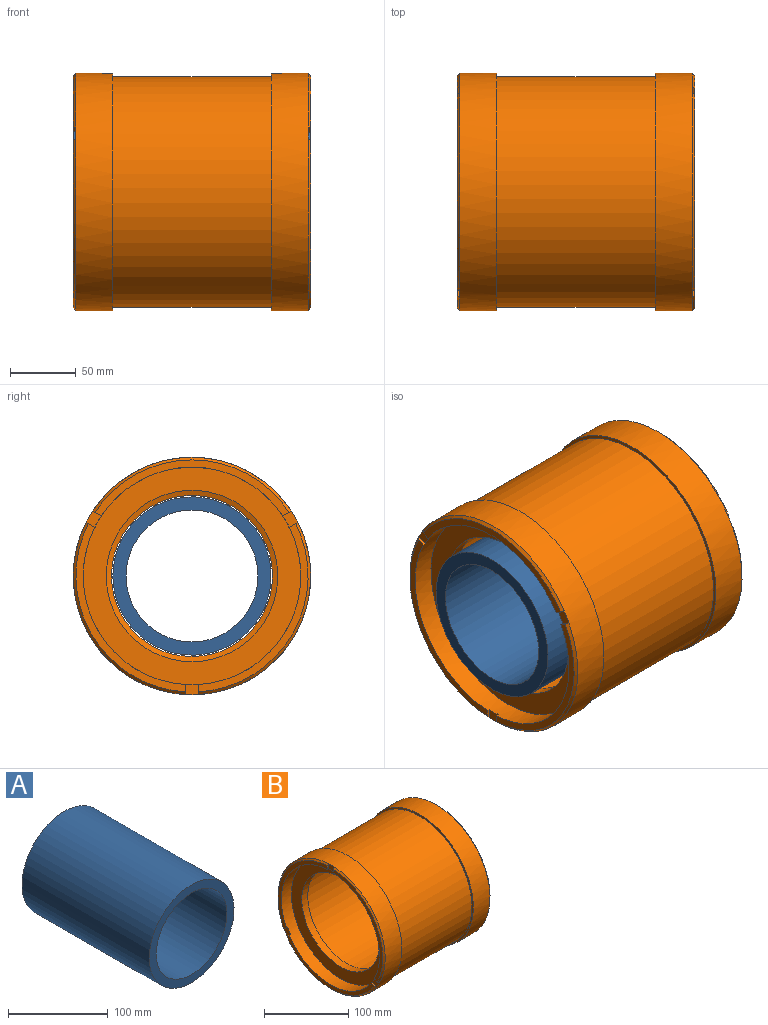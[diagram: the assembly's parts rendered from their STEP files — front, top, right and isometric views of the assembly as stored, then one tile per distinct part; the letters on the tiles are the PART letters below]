
ASSEMBLY  parts=2 mates=1
PART A: 4 faces, bbox 120x180x120 mm
  f0: cylinder r=50mm len=180mm, axis (0,1,0), area 56548.7mm2, adj f2,f3
  f1: cylinder r=60mm len=180mm, axis (0,1,0), area 67858.4mm2, adj f2,f3
  f2: plane 120x120mm, normal (0,-1,0), area 3455.8mm2, adj f0,f1
  f3: plane 120x120mm, normal (0,1,0), area 3455.8mm2, adj f0,f1
PART B: 45 faces, bbox 180x180x180 mm
  f0: plane 127.46x83mm, normal (-1,0,0), area 927mm2, adj f2,f13,f39,f43
  f1: plane 147.17x42.5mm, normal (-1,0,0), area 927mm2, adj f3,f13,f36,f40
  f2: cone r=88mm half-angle=45deg, axis (1,0,0), area 498.9mm2, adj f0,f25,f39,f43
  f3: cone r=88mm half-angle=45deg, axis (1,0,0), area 498.9mm2, adj f1,f25,f36,f40
  f4: cone r=82.5mm half-angle=45deg, axis (1,0,0), area 3469.2mm2, adj f5,f6,f7,f8,f20,f28,f29,f30
  f5: cone r=82.5mm half-angle=45deg, axis (1,0,0), area 0.2mm2, adj f4,f8,f27
  f6: plane 127.46x83mm, normal (1,0,0), area 927mm2, adj f4,f9,f28,f33
  f7: plane 127.46x83mm, normal (1,0,0), area 927mm2, adj f4,f10,f30,f34
  f8: plane 147.17x42.5mm, normal (1,0,0), area 927mm2, adj f4,f5,f11,f27,f31
  f9: cone r=90mm half-angle=45deg, axis (-1,0,0), area 498.9mm2, adj f6,f21,f28,f33
  f10: cone r=90mm half-angle=45deg, axis (-1,0,0), area 498.9mm2, adj f7,f21,f30,f34
  f11: cone r=90mm half-angle=45deg, axis (-1,0,0), area 498.9mm2, adj f8,f21,f27,f31
  f12: plane 127.46x83mm, normal (-1,0,0), area 927mm2, adj f13,f26,f37,f42
  f13: cylinder r=82.5mm len=165mm, axis (-1,0,0), area 8752.1mm2, adj f0,f1,f12,f14,f36,f37,f38,f39
  f14: plane 165x165mm, normal (-1,0,0), area 8109.2mm2, adj f13,f15
  f15: cylinder r=65mm len=130mm, axis (-1,0,0), area 4084.1mm2, adj f14,f16
  f16: cone r=77.5mm half-angle=70deg, axis (1,0,0), area 5955.1mm2, adj f15,f17
  f17: cylinder r=77.5mm len=155mm, axis (-1,0,0), area 64006.7mm2, adj f16,f18
  f18: cone r=61mm half-angle=70deg, axis (-1,0,0), area 7640.1mm2, adj f17,f19
  f19: cylinder r=61mm len=122mm, axis (-1,0,0), area 2299.6mm2, adj f18,f20
  f20: plane 155x155mm, normal (1,0,0), area 7179.3mm2, adj f4,f19
  f21: cylinder r=90mm len=180mm, axis (-1,0,0), area 15833.6mm2, adj f9,f10,f11,f22,f29,f32,f35
  f22: plane 180x180mm, normal (-1,0,0), area 1394.1mm2, adj f21,f23
  f23: cylinder r=87.5mm len=175mm, axis (-1,0,0), area 65973.4mm2, adj f22,f24
  f24: plane 180x180mm, normal (1,0,0), area 1394.1mm2, adj f23,f25
  f25: cylinder r=90mm len=180mm, axis (-1,0,0), area 15833.6mm2, adj f2,f3,f24,f26,f38,f41,f44
  f26: cone r=88mm half-angle=45deg, axis (1,0,0), area 498.9mm2, adj f12,f25,f37,f42
  f27: plane 8.24x4.76mm, normal (0,-0.5,0.87), area 15mm2, adj f5,f8,f11,f29
  f28: plane 8.24x4.76mm, normal (0,0.5,-0.87), area 15mm2, adj f4,f6,f9,f29
  f29: plane 13.42x13.24mm, normal (1,0,0), area 95.1mm2, adj f4,f21,f27,f28
  f30: plane 8.24x4.76mm, normal (0,-0.5,-0.87), area 15mm2, adj f4,f7,f10,f32
  f31: plane 8.24x4.76mm, normal (0,0.5,0.87), area 15mm2, adj f4,f8,f11,f32
  f32: plane 13.42x13.24mm, normal (1,0,0), area 95.1mm2, adj f4,f21,f30,f31
  f33: plane 9.52x2mm, normal (0,1,0), area 15mm2, adj f4,f6,f9,f35
  f34: plane 9.52x2mm, normal (0,-1,0), area 15mm2, adj f4,f7,f10,f35
  f35: plane 10x9.66mm, normal (1,0,0), area 95.1mm2, adj f4,f21,f33,f34
  f36: plane 6.51x3.76mm, normal (0,-0.5,0.87), area 13mm2, adj f1,f3,f13,f38
  f37: plane 6.51x3.76mm, normal (0,0.5,-0.87), area 13mm2, adj f12,f13,f26,f38
  f38: plane 12.42x11.51mm, normal (-1,0,0), area 75mm2, adj f13,f25,f36,f37
  f39: plane 6.51x3.76mm, normal (0,-0.5,-0.87), area 13mm2, adj f0,f2,f13,f41
  f40: plane 6.51x3.76mm, normal (0,0.5,0.87), area 13mm2, adj f1,f3,f13,f41
  f41: plane 12.42x11.51mm, normal (-1,0,0), area 75mm2, adj f13,f25,f39,f40
  f42: plane 7.51x2mm, normal (0,1,0), area 13mm2, adj f12,f13,f26,f44
  f43: plane 7.51x2mm, normal (0,-1,0), area 13mm2, adj f0,f2,f13,f44
  f44: plane 10x7.65mm, normal (-1,0,0), area 75mm2, adj f13,f25,f42,f43
PLACE A rot(axis=(0.58,-0.58,0.58),120deg) t=(72.21,39.37,-144.64)mm
PLACE B rot(axis=(1,0,0),180deg) t=(103.27,39.37,-144.64)mm
MATE cylindrical B.f2 <-> A.f0  axis (1,0,0) through (252.21,39.37,-144.64)mm
